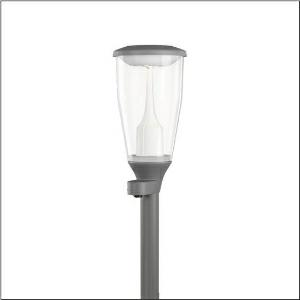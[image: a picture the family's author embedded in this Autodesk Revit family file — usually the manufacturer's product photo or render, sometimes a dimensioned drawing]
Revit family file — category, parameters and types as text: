
# Revit family: dl_11_iq___st1_2a_5xa5575eu14h000022_29dc
name_source: partatom
category: Lighting Fixtures
units: mm (PartAtom-declared; Revit-internal decimal feet)

## family parameters
Cut with Voids When Loaded = No
Host = Face
Light Source = No
Part Type = Normal
Room Calculation Point = No
Round Connector Dimension = Use Diameter
Shared = No

## types (1)
- --- (1 x LED, 1560 lm, 10.7 W, 3000K)
    Apparent Load = 11 VA
    CIE Flux Codes = 24 63 94 96 100
    Color Rendering = 70
    Color Temperature = 3000K
    Default Elevation = 1800 mm
    Description = DL 11 iQ, mast luminaire, Module 540 iQ-SR, primary light control with 3 zone facetted reflector, of plastic, silver coated, highly specular, structured, primary optical cover: cover, of PMMA, transparent, light distribution: ST1.2a, light emission: direct distribution, primary light characteristic: asymmetric, installation type: post-top, LED, High Power LED, rated luminous flux: 1.560lm, luminous efficacy: 146lm/W, light colour: 730, colour temperature: 3000K, control gear: iQ-Street Remote, D4i with power reduction, control: pre-setting: logarithmic dimming characteristic, Street-Remote, Auto-Match, Temp-Guard, Lumen-Switch, Night-Set, Smart-Wire, Light-Fading, Desk-Remote (wireless, voltage-free reading and setting of iQ features in the workshop via application-optimized NFC function/RFID function), optimised constant luminous flux control (CLO 2.0), mains connection: 220..240V, AC, 50/60Hz, connection cable pre-assembled, cable length: 5,5m, start of lifetime: 11W, end of service life: 11W, reduction: 6W, luminaire housing, upper part, of diecast aluminium, coated, SITECO metallic grey (DB 702S), spigot size: 76mm (post-top), mounting height: 3..5m, post-top mast mounting element, of diecast aluminium, coated, SITECO metallic grey (DB 702S), Module 540 iQ-SR, traffic white (RAL 9016), equipment: standard, Smart Interface below, protection rating (complete): IP66, insulation class (complete): insulation class II (safety insulation), certification: CE, ENEC, ENEC+, VDE, impact resistance: IK07, packaging unit: 1 piece

Light Distribution: ST1.2a
    Height = 665 mm
    Lamp = 1 x LED
    Lamp Light Flux = 1560 lm
    Lamp Power = 10.7 W
    Lamp count = 1
    Length = 334 mm
    Luminous efficacy = 146 lm/W
    Manufacturer = Siteco
    ModVariant = No
    Model = 5XA5575EU14H000022
    Number of Poles = 1
    OnlyDefault = Yes
    Power Factor = 1
    Product Name = DL 11 iQ | ST1.2a
    Product group = mast luminaire | pylon top
    ProductGroupID = 6100
    Protection Class = Protection class II
    Protection Degree = IP 66
    RLX_Detail_Level = 1
    RLX_Emergency_Light_Flux = 0 lm
    RLX_Emergency_Type = 0
    RLX_Emergency_Type_DB = No
    RlxData = <blob elided: 160409 chars, md5=726b8589>
    Socket = socket
    Standby Power = 0 W
    System Light Flux = 1560 lm
    System Power = 11 W
    Type Comments = factory setting: luminous flux: 100 % | dim-lin: 254 | 419 mA
    Type Image = l_1337539.jpg
    URL = http://relux.com
    VarID = @adj_098723
    Voltage = 0 V
    Weight = 0.00 kg
    Width = 0 mm  [stored 0 ft]

note: [stored X ft] marks values corroborated as IEEE doubles in the binary element streams (Revit-internal decimal feet)

## geometry (parser evidence)
native form markers: Blend x4, Sweep x12
no freeform markers — native parametric forms only
